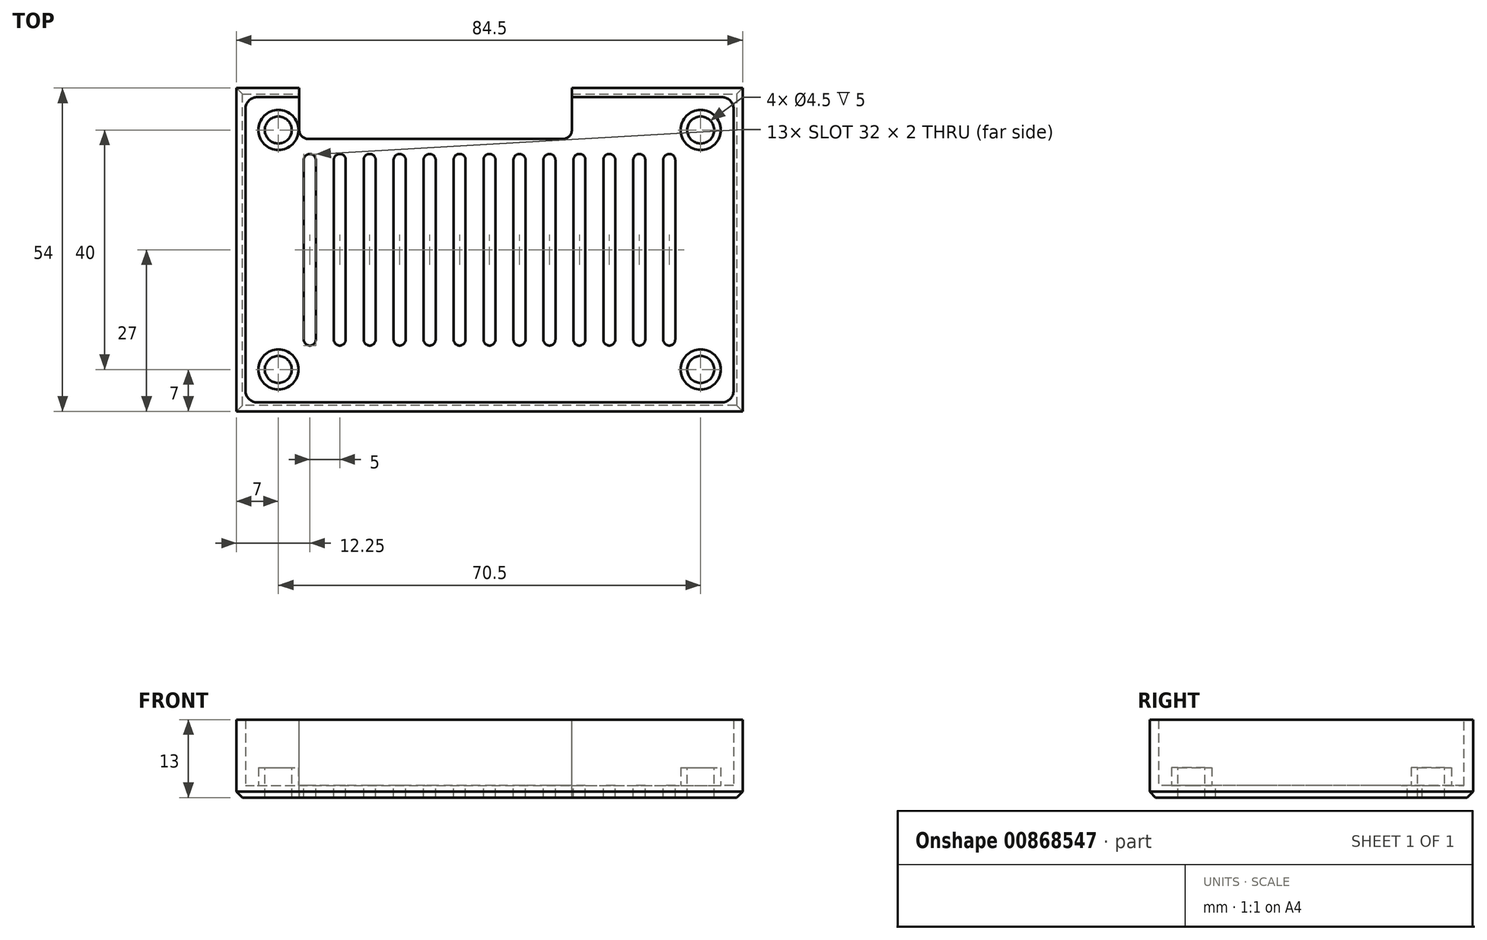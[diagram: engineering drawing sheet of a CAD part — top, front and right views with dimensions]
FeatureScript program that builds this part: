
annotation { "Feature Type Name" : "Feature", "Feature Type Description" : "" }
export const myFeature = defineFeature(function(context is Context, id is Id, definition is map)
    precondition{}
    {
        {
            var Q0;
            Q0=qCreatedBy(makeId("Top.planeOp"),FACE);
            var sketch = newSketch(context, id + "F0", { "sketchPlane" : qUnion([Q0])});
            skLineSegment(sketch, "E0.bottom", {"start": v(-38.75, 23.5) * mm, "end": v(38.75, 23.5) * mm, "construction": true});
            skLineSegment(sketch, "E0.top", {"start": v(-38.75, -23.5) * mm, "end": v(38.75, -23.5) * mm, "construction": true});
            skLineSegment(sketch, "E0.left", {"start": v(-38.75, 23.5) * mm, "end": v(-38.75, -23.5) * mm, "construction": true});
            skLineSegment(sketch, "E0.right", {"start": v(38.75, 23.5) * mm, "end": v(38.75, -23.5) * mm, "construction": true});
            skCircle(sketch, "E1", {"center": v(-35.25, 20) * mm, "radius": 2.2 * mm});
            skLineSegment(sketch, "E2", {"start": v(0, 23.5) * mm, "end": v(0, -23.5) * mm, "construction": true});
            skLineSegment(sketch, "E3.bottom", {"start": v(-30.75, 23.5) * mm, "end": v(9.25, 23.5) * mm, "construction": true});
            skLineSegment(sketch, "E3.top", {"start": v(-30.75, 19.5) * mm, "end": v(9.25, 19.5) * mm, "construction": true});
            skLineSegment(sketch, "E3.left", {"start": v(-30.75, 23.5) * mm, "end": v(-30.75, 19.5) * mm, "construction": true});
            skLineSegment(sketch, "E3.right", {"start": v(9.25, 23.5) * mm, "end": v(9.25, 19.5) * mm, "construction": true});
            skPoint(sketch, "E4.visualSharp", {"position": v(-38.75, 23.5) * mm});
            skLineSegment(sketch, "E5", {"start": v(-38.75, 0) * mm, "end": v(38.75, 0) * mm, "construction": true});
            skCircle(sketch, "E6.MirrorC", {"center": v(-35.25, -20) * mm, "radius": 2.2 * mm});
            skCircle(sketch, "E7.MirrorC", {"center": v(35.25, 20) * mm, "radius": 2.2 * mm});
            skCircle(sketch, "E8.MirrorC", {"center": v(35.25, -20) * mm, "radius": 2.2 * mm});
            skLineSegment(sketch, "E9.0", {"start": v(-40.75, 23.5) * mm, "end": v(-40.75, -23.5) * mm});
            skLineSegment(sketch, "E9.1", {"start": v(-38.75, 25.5) * mm, "end": v(38.75, 25.5) * mm});
            skLineSegment(sketch, "E9.2", {"start": v(40.75, 23.5) * mm, "end": v(40.75, -23.5) * mm});
            skLineSegment(sketch, "E9.3", {"start": v(-38.75, -25.5) * mm, "end": v(38.75, -25.5) * mm});
            skLineSegment(sketch, "E10.0", {"start": v(-42.25, -27) * mm, "end": v(42.25, -27) * mm});
            skLineSegment(sketch, "E10.1", {"start": v(-42.25, 27) * mm, "end": v(-42.25, -27) * mm});
            skLineSegment(sketch, "E10.2", {"start": v(-42.25, 27) * mm, "end": v(42.25, 27) * mm});
            skLineSegment(sketch, "E10.3", {"start": v(42.25, 27) * mm, "end": v(42.25, -27) * mm});
            skPoint(sketch, "E11.visualSharp", {"position": v(-40.75, 25.5) * mm});
            skArc(sketch, "E11.filletArc", {"start": v(-38.75, 25.5) * mm, "mid": v(-40.16, 24.91) * mm, "end": v(-40.75, 23.5) * mm});
            skPoint(sketch, "E12.visualSharp", {"position": v(-40.75, -25.5) * mm});
            skArc(sketch, "E12.filletArc", {"start": v(-40.75, -23.5) * mm, "mid": v(-40.16, -24.91) * mm, "end": v(-38.75, -25.5) * mm});
            skPoint(sketch, "E13.visualSharp", {"position": v(40.75, -25.5) * mm});
            skArc(sketch, "E13.filletArc", {"start": v(38.75, -25.5) * mm, "mid": v(40.16, -24.91) * mm, "end": v(40.75, -23.5) * mm});
            skPoint(sketch, "E14.visualSharp", {"position": v(40.75, 25.5) * mm});
            skArc(sketch, "E14.filletArc", {"start": v(40.75, 23.5) * mm, "mid": v(40.16, 24.91) * mm, "end": v(38.75, 25.5) * mm});
            skSolve(sketch);
        }
        {
            var Q0;
            Q0 = qSketchRegion(id + "F0", true);
            extrude(context, id + "F1", {"entities" : qUnion([Q0]), "depth" : 11 * mm, "offsetDistance" : 25 * mm});
        }
        {
            var Q0;
            Q0=makeQuery(id+"F1.opExtrude","CAP_FACE",FACE,{"disambiguationData":[OSD([sQuery(id+"F0.wireOp",EDGE,"E9.0"),sQuery(id+"F0.wireOp",EDGE,"E9.1"),sQuery(id+"F0.wireOp",EDGE,"E9.2"),sQuery(id+"F0.wireOp",EDGE,"E9.3"),sQuery(id+"F0.wireOp",EDGE,"E10.0"),sQuery(id+"F0.wireOp",EDGE,"E10.1"),sQuery(id+"F0.wireOp",EDGE,"E10.2"),sQuery(id+"F0.wireOp",EDGE,"E10.3")])],"isStart":true});
            var sketch = newSketch(context, id + "F2", { "sketchPlane" : qUnion([Q0])});
            skLineSegment(sketch, "E15.bottom", {"start": v(-42.25, 27) * mm, "end": v(42.25, 27) * mm});
            skLineSegment(sketch, "E15.top", {"start": v(-42.25, -27) * mm, "end": v(42.25, -27) * mm});
            skLineSegment(sketch, "E15.left", {"start": v(-42.25, 27) * mm, "end": v(-42.25, -27) * mm});
            skLineSegment(sketch, "E15.right", {"start": v(42.25, 27) * mm, "end": v(42.25, -27) * mm});
            skSolve(sketch);
        }
        {
            var Q0;
            Q0 = qSketchRegion(id + "F2", true);
            extrude(context, id + "F3", {"entities" : qUnion([Q0]), "operationType" : NewBodyOperationType.ADD, "depth" : 2 * mm, "offsetDistance" : 25 * mm});
        }
        {
            var Q0;
            Q0=makeQuery(id+"F3.opExtrude","CAP_FACE",FACE,{"disambiguationData":[OSD([sQuery(id+"F2.wireOp",EDGE,"E15.bottom"),sQuery(id+"F2.wireOp",EDGE,"E15.top"),sQuery(id+"F2.wireOp",EDGE,"E15.left"),sQuery(id+"F2.wireOp",EDGE,"E15.right")])],"isStart":true});
            var sketch = newSketch(context, id + "F4", { "sketchPlane" : qUnion([Q0])});
            skLineSegment(sketch, "E16.bottom", {"start": v(-38.75, 23.5) * mm, "end": v(38.75, 23.5) * mm, "construction": true});
            skLineSegment(sketch, "E16.top", {"start": v(-38.75, -23.5) * mm, "end": v(38.75, -23.5) * mm, "construction": true});
            skLineSegment(sketch, "E16.left", {"start": v(-38.75, 23.5) * mm, "end": v(-38.75, -23.5) * mm, "construction": true});
            skLineSegment(sketch, "E16.right", {"start": v(38.75, 23.5) * mm, "end": v(38.75, -23.5) * mm, "construction": true});
            skCircle(sketch, "E17", {"center": v(-35.25, 20) * mm, "radius": 2.25 * mm});
            skLineSegment(sketch, "E18", {"start": v(0, 23.5) * mm, "end": v(0, -23.5) * mm, "construction": true});
            skLineSegment(sketch, "E19.top", {"start": v(-30.25, 18.5) * mm, "end": v(12.25, 18.5) * mm});
            skPoint(sketch, "E20.visualSharp", {"position": v(-38.75, 23.5) * mm});
            skLineSegment(sketch, "E21", {"start": v(-38.75, 0) * mm, "end": v(38.75, 0) * mm, "construction": true});
            skCircle(sketch, "E22.MirrorC", {"center": v(-35.25, -20) * mm, "radius": 2.25 * mm});
            skCircle(sketch, "E23.MirrorC", {"center": v(35.25, 20) * mm, "radius": 2.25 * mm});
            skCircle(sketch, "E24.MirrorC", {"center": v(35.25, -20) * mm, "radius": 2.25 * mm});
            skLineSegment(sketch, "E25", {"start": v(-31.75, 27) * mm, "end": v(13.75, 27) * mm});
            skLineSegment(sketch, "E26", {"start": v(-31.75, 27) * mm, "end": v(-31.75, 20) * mm});
            skLineSegment(sketch, "E27", {"start": v(13.75, 27) * mm, "end": v(13.75, 20) * mm});
            skPoint(sketch, "E28.visualSharp", {"position": v(-31.75, 18.5) * mm});
            skArc(sketch, "E28.filletArc", {"start": v(-31.75, 20) * mm, "mid": v(-31.31, 18.94) * mm, "end": v(-30.25, 18.5) * mm});
            skPoint(sketch, "E29.visualSharp", {"position": v(13.75, 18.5) * mm});
            skArc(sketch, "E29.filletArc", {"start": v(12.25, 18.5) * mm, "mid": v(13.31, 18.94) * mm, "end": v(13.75, 20) * mm});
            skSolve(sketch);
        }
        {
            var Q0;
            Q0 = qSketchRegion(id + "F4", true);
            var Q1;
            Q1=makeQuery(id+"F3.opExtrude","CAP_FACE",FACE,{"disambiguationData":[OSD([sQuery(id+"F2.wireOp",EDGE,"E15.bottom"),sQuery(id+"F2.wireOp",EDGE,"E15.top"),sQuery(id+"F2.wireOp",EDGE,"E15.left"),sQuery(id+"F2.wireOp",EDGE,"E15.right")])],"isStart":false});
            extrude(context, id + "F5", {"entities" : qUnion([Q0]), "operationType" : NewBodyOperationType.REMOVE, "endBound" : BoundingType.SYMMETRIC, "oppositeDirection" : true, "depth" : 25 * mm, "endBoundEntityFace" : qUnion([Q1]), "offsetDistance" : 25 * mm});
        }
        {
            var Q0;
            Q0=makeQuery(id+"F3.opExtrude","CAP_FACE",FACE,{"disambiguationData":[OSD([sQuery(id+"F2.wireOp",EDGE,"E15.bottom"),sQuery(id+"F2.wireOp",EDGE,"E15.top"),sQuery(id+"F2.wireOp",EDGE,"E15.left"),sQuery(id+"F2.wireOp",EDGE,"E15.right")])],"isStart":true});
            var sketch = newSketch(context, id + "F6", { "sketchPlane" : qUnion([Q0])});
            skCircle(sketch, "E30", {"center": v(-35.25, 20) * mm, "radius": 3.35 * mm});
            skCircle(sketch, "E31", {"center": v(-35.25, 20) * mm, "radius": 2.25 * mm});
            skCircle(sketch, "E32.MirrorC", {"center": v(35.25, 20) * mm, "radius": 2.25 * mm});
            skCircle(sketch, "E33.MirrorC", {"center": v(35.25, 20) * mm, "radius": 3.35 * mm});
            skCircle(sketch, "E34.MirrorC", {"center": v(-35.25, -20) * mm, "radius": 3.35 * mm});
            skCircle(sketch, "E35.MirrorC", {"center": v(35.25, -20) * mm, "radius": 2.25 * mm});
            skCircle(sketch, "E36.MirrorC", {"center": v(-35.25, -20) * mm, "radius": 2.25 * mm});
            skCircle(sketch, "E37.MirrorC", {"center": v(35.25, -20) * mm, "radius": 3.35 * mm});
            skSolve(sketch);
        }
        {
            var Q0;
            Q0 = qSketchRegion(id + "F6", true);
            extrude(context, id + "F7", {"entities" : qUnion([Q0]), "operationType" : NewBodyOperationType.ADD, "depth" : 3 * mm, "offsetDistance" : 25 * mm});
        }
        {
            var Q0;
            Q0=makeQuery(id+"F3.opExtrude","CAP_EDGE",EDGE,{"disambiguationData":[OSD([sQuery(id+"F2.wireOp",EDGE,"E15.left")])],"isStart":false});
            var Q1;
            {var subQ0=sQuery(id+"F2.wireOp",EDGE,"E15.top");Q1=makeQuery(id+"F5.boolean.opBoolean","SPLIT",EDGE,{"disambiguationData":[TD([makeQuery(id+"F1.opExtrude","SWEPT_FACE",FACE,{"disambiguationData":[OSD([sQuery(id+"F0.wireOp",EDGE,"E10.1")])]})])],"derivedFrom":makeQuery(id+"F3.opExtrude","CAP_EDGE",EDGE,{"disambiguationData":[OSD([subQ0])],"isStart":false})});}
            var Q2;
            Q2=makeQuery(id+"F3.opExtrude","CAP_EDGE",EDGE,{"disambiguationData":[OSD([sQuery(id+"F2.wireOp",EDGE,"E15.bottom")])],"isStart":false});
            var Q3;
            Q3=makeQuery(id+"F3.opExtrude","CAP_EDGE",EDGE,{"disambiguationData":[OSD([sQuery(id+"F2.wireOp",EDGE,"E15.right")])],"isStart":false});
            var Q4;
            {var subQ0=sQuery(id+"F2.wireOp",EDGE,"E15.top");Q4=makeQuery(id+"F5.boolean.opBoolean","SPLIT",EDGE,{"disambiguationData":[TD([makeQuery(id+"F1.opExtrude","SWEPT_FACE",FACE,{"disambiguationData":[OSD([sQuery(id+"F0.wireOp",EDGE,"E10.3")])]})])],"derivedFrom":makeQuery(id+"F3.opExtrude","CAP_EDGE",EDGE,{"disambiguationData":[OSD([subQ0])],"isStart":false})});}
            chamfer(context, id + "F8", {"entities" : qUnion([Q0, Q1, Q2, Q3, Q4]), "width" : 1 * mm, "tangentPropagation" : true});
        }
        {
            var Q0;
            Q0=makeQuery(id+"F7.boolean.opBoolean","SPLIT",FACE,{"disambiguationData":[TD([makeQuery(id+"F1.opExtrude","SWEPT_FACE",FACE,{"disambiguationData":[OSD([sQuery(id+"F0.wireOp",EDGE,"E9.0")])]})])],"derivedFrom":makeQuery(id+"F3.opExtrude","CAP_FACE",FACE,{"disambiguationData":[OSD([sQuery(id+"F2.wireOp",EDGE,"E15.bottom"),sQuery(id+"F2.wireOp",EDGE,"E15.top"),sQuery(id+"F2.wireOp",EDGE,"E15.left"),sQuery(id+"F2.wireOp",EDGE,"E15.right")])],"isStart":true})});
            var sketch = newSketch(context, id + "F9", { "sketchPlane" : qUnion([Q0])});
            skLineSegment(sketch, "E38.left", {"start": v(-1, 15) * mm, "end": v(-1, -15) * mm});
            skLineSegment(sketch, "E38.right", {"start": v(1, 15) * mm, "end": v(1, -15) * mm});
            skLineSegment(sketch, "E39", {"start": v(1, 15) * mm, "end": v(-1, -15) * mm, "construction": true});
            skArc(sketch, "E40", {"start": v(1, 15) * mm, "mid": v(0, 16) * mm, "end": v(-1, 15) * mm});
            skArc(sketch, "E41", {"start": v(-1, -15) * mm, "mid": v(0, -16) * mm, "end": v(1, -15) * mm});
            skArc(sketch, "E42.1.0.0", {"start": v(6, 15) * mm, "mid": v(5, 16) * mm, "end": v(4, 15) * mm});
            skLineSegment(sketch, "E42.1.0.1", {"start": v(4, 15) * mm, "end": v(4, -15) * mm});
            skLineSegment(sketch, "E42.1.0.2", {"start": v(6, 15) * mm, "end": v(6, -15) * mm});
            skArc(sketch, "E42.1.0.3", {"start": v(4, -15) * mm, "mid": v(5, -16) * mm, "end": v(6, -15) * mm});
            skArc(sketch, "E42.2.0.0", {"start": v(11, 15) * mm, "mid": v(10, 16) * mm, "end": v(9, 15) * mm});
            skLineSegment(sketch, "E42.2.0.1", {"start": v(9, 15) * mm, "end": v(9, -15) * mm});
            skLineSegment(sketch, "E42.2.0.2", {"start": v(11, 15) * mm, "end": v(11, -15) * mm});
            skArc(sketch, "E42.2.0.3", {"start": v(9, -15) * mm, "mid": v(10, -16) * mm, "end": v(11, -15) * mm});
            skArc(sketch, "E42.3.0.0", {"start": v(16, 15) * mm, "mid": v(15, 16) * mm, "end": v(14, 15) * mm});
            skLineSegment(sketch, "E42.3.0.1", {"start": v(14, 15) * mm, "end": v(14, -15) * mm});
            skLineSegment(sketch, "E42.3.0.2", {"start": v(16, 15) * mm, "end": v(16, -15) * mm});
            skArc(sketch, "E42.3.0.3", {"start": v(14, -15) * mm, "mid": v(15, -16) * mm, "end": v(16, -15) * mm});
            skArc(sketch, "E42.4.0.0", {"start": v(21, 15) * mm, "mid": v(20, 16) * mm, "end": v(19, 15) * mm});
            skLineSegment(sketch, "E42.4.0.1", {"start": v(19, 15) * mm, "end": v(19, -15) * mm});
            skLineSegment(sketch, "E42.4.0.2", {"start": v(21, 15) * mm, "end": v(21, -15) * mm});
            skArc(sketch, "E42.4.0.3", {"start": v(19, -15) * mm, "mid": v(20, -16) * mm, "end": v(21, -15) * mm});
            skArc(sketch, "E42.5.0.0", {"start": v(26, 15) * mm, "mid": v(25, 16) * mm, "end": v(24, 15) * mm});
            skLineSegment(sketch, "E42.5.0.1", {"start": v(24, 15) * mm, "end": v(24, -15) * mm});
            skLineSegment(sketch, "E42.5.0.2", {"start": v(26, 15) * mm, "end": v(26, -15) * mm});
            skArc(sketch, "E42.5.0.3", {"start": v(24, -15) * mm, "mid": v(25, -16) * mm, "end": v(26, -15) * mm});
            skLineSegment(sketch, "E42.direction1", {"start": v(-1, -15) * mm, "end": v(4, -15) * mm, "construction": true});
            skLineSegment(sketch, "E43.1.0.0", {"start": v(-4, 15) * mm, "end": v(-6, -15) * mm, "construction": true});
            skArc(sketch, "E43.1.0.1", {"start": v(-4, 15) * mm, "mid": v(-5, 16) * mm, "end": v(-6, 15) * mm});
            skArc(sketch, "E43.1.0.2", {"start": v(-6, -15) * mm, "mid": v(-5, -16) * mm, "end": v(-4, -15) * mm});
            skLineSegment(sketch, "E43.1.0.3", {"start": v(-6, 15) * mm, "end": v(-6, -15) * mm});
            skLineSegment(sketch, "E43.1.0.4", {"start": v(-4, 15) * mm, "end": v(-4, -15) * mm});
            skLineSegment(sketch, "E43.2.0.0", {"start": v(-9, 15) * mm, "end": v(-11, -15) * mm, "construction": true});
            skArc(sketch, "E43.2.0.1", {"start": v(-9, 15) * mm, "mid": v(-10, 16) * mm, "end": v(-11, 15) * mm});
            skArc(sketch, "E43.2.0.2", {"start": v(-11, -15) * mm, "mid": v(-10, -16) * mm, "end": v(-9, -15) * mm});
            skLineSegment(sketch, "E43.2.0.3", {"start": v(-11, 15) * mm, "end": v(-11, -15) * mm});
            skLineSegment(sketch, "E43.2.0.4", {"start": v(-9, 15) * mm, "end": v(-9, -15) * mm});
            skLineSegment(sketch, "E43.3.0.0", {"start": v(-14, 15) * mm, "end": v(-16, -15) * mm, "construction": true});
            skArc(sketch, "E43.3.0.1", {"start": v(-14, 15) * mm, "mid": v(-15, 16) * mm, "end": v(-16, 15) * mm});
            skArc(sketch, "E43.3.0.2", {"start": v(-16, -15) * mm, "mid": v(-15, -16) * mm, "end": v(-14, -15) * mm});
            skLineSegment(sketch, "E43.3.0.3", {"start": v(-16, 15) * mm, "end": v(-16, -15) * mm});
            skLineSegment(sketch, "E43.3.0.4", {"start": v(-14, 15) * mm, "end": v(-14, -15) * mm});
            skLineSegment(sketch, "E43.4.0.0", {"start": v(-19, 15) * mm, "end": v(-21, -15) * mm, "construction": true});
            skArc(sketch, "E43.4.0.1", {"start": v(-19, 15) * mm, "mid": v(-20, 16) * mm, "end": v(-21, 15) * mm});
            skArc(sketch, "E43.4.0.2", {"start": v(-21, -15) * mm, "mid": v(-20, -16) * mm, "end": v(-19, -15) * mm});
            skLineSegment(sketch, "E43.4.0.3", {"start": v(-21, 15) * mm, "end": v(-21, -15) * mm});
            skLineSegment(sketch, "E43.4.0.4", {"start": v(-19, 15) * mm, "end": v(-19, -15) * mm});
            skLineSegment(sketch, "E43.5.0.0", {"start": v(-24, 15) * mm, "end": v(-26, -15) * mm, "construction": true});
            skArc(sketch, "E43.5.0.1", {"start": v(-24, 15) * mm, "mid": v(-25, 16) * mm, "end": v(-26, 15) * mm});
            skArc(sketch, "E43.5.0.2", {"start": v(-26, -15) * mm, "mid": v(-25, -16) * mm, "end": v(-24, -15) * mm});
            skLineSegment(sketch, "E43.5.0.3", {"start": v(-26, 15) * mm, "end": v(-26, -15) * mm});
            skLineSegment(sketch, "E43.5.0.4", {"start": v(-24, 15) * mm, "end": v(-24, -15) * mm});
            skLineSegment(sketch, "E43.direction1", {"start": v(-1, -15) * mm, "end": v(-6, -15) * mm, "construction": true});
            skLineSegment(sketch, "E44.0.6.0", {"start": v(-29, 15) * mm, "end": v(-31, -15) * mm, "construction": true});
            skArc(sketch, "E44.3.6.0", {"start": v(-29, 15) * mm, "mid": v(-30, 16) * mm, "end": v(-31, 15) * mm});
            skArc(sketch, "E44.7.6.0", {"start": v(-31, -15) * mm, "mid": v(-30, -16) * mm, "end": v(-29, -15) * mm});
            skLineSegment(sketch, "E44.11.6.0", {"start": v(-31, 15) * mm, "end": v(-31, -15) * mm});
            skLineSegment(sketch, "E44.14.6.0", {"start": v(-29, 15) * mm, "end": v(-29, -15) * mm});
            skArc(sketch, "E45.0.6.0", {"start": v(31, 15) * mm, "mid": v(30, 16) * mm, "end": v(29, 15) * mm});
            skLineSegment(sketch, "E45.4.6.0", {"start": v(29, 15) * mm, "end": v(29, -15) * mm});
            skLineSegment(sketch, "E45.7.6.0", {"start": v(31, 15) * mm, "end": v(31, -15) * mm});
            skArc(sketch, "E45.10.6.0", {"start": v(29, -15) * mm, "mid": v(30, -16) * mm, "end": v(31, -15) * mm});
            skSolve(sketch);
        }
        {
            var Q0;
            Q0 = qSketchRegion(id + "F9", true);
            var Q1;
            Q1=makeQuery(id+"F3.opExtrude","CAP_FACE",FACE,{"disambiguationData":[OSD([sQuery(id+"F2.wireOp",EDGE,"E15.bottom"),sQuery(id+"F2.wireOp",EDGE,"E15.top"),sQuery(id+"F2.wireOp",EDGE,"E15.left"),sQuery(id+"F2.wireOp",EDGE,"E15.right")])],"isStart":false});
            extrude(context, id + "F10", {"entities" : qUnion([Q0]), "operationType" : NewBodyOperationType.REMOVE, "endBound" : BoundingType.UP_TO_SURFACE, "oppositeDirection" : true, "depth" : 25 * mm, "endBoundEntityFace" : qUnion([Q1]), "offsetDistance" : 25 * mm});
        }
    });
